# Revit family: TYCO-FPP-FireClass-FC410LI LINE ISOLATOR MODULE
name_source: partatom
category: Electrical Fixtures
revit_build: Autodesk Revit 2014 (Build: 20130308_1515(x64)
units: mm (PartAtom-declared; Revit-internal decimal feet)

## types (1)
- TYCO-FPP-FireClass-FC410LI LINE ISOLATOR MODULE
    Description = Line Isolation
Module
    Equivalent Capacitance = 0.5nF
    Front Cover = Yes
    Input Current = 80μA
    Keynote = FC410LI
    Length = 60 mm
    Loop Voltage = 20V to 40Vdc
    Manufacturer = Tyco
    Model = FireClass - 545.800.004
    Operating Temperature = - 20 - + 70 ºC
    PCB = PCB
    Rear Cover = Yes
    Relative Humidity = 10% to 95%
    Series Resistance (max.) = 0.25 Ohm
    Storage Temperature = –40°C to +80°C
    Thickness = 2 mm
    Type Comments = It monitors the line condition
and when detecting a short circuit will isolate the affected section whilst
allowing the rest of the loop to function normally.
    URL = https://fireclass.co.uk
    Width = 84 mm
    Wire Size (maximum) = 2.5sq. mm

## geometry (parser evidence)
native form markers: Sweep x8
no freeform markers — native parametric forms only
